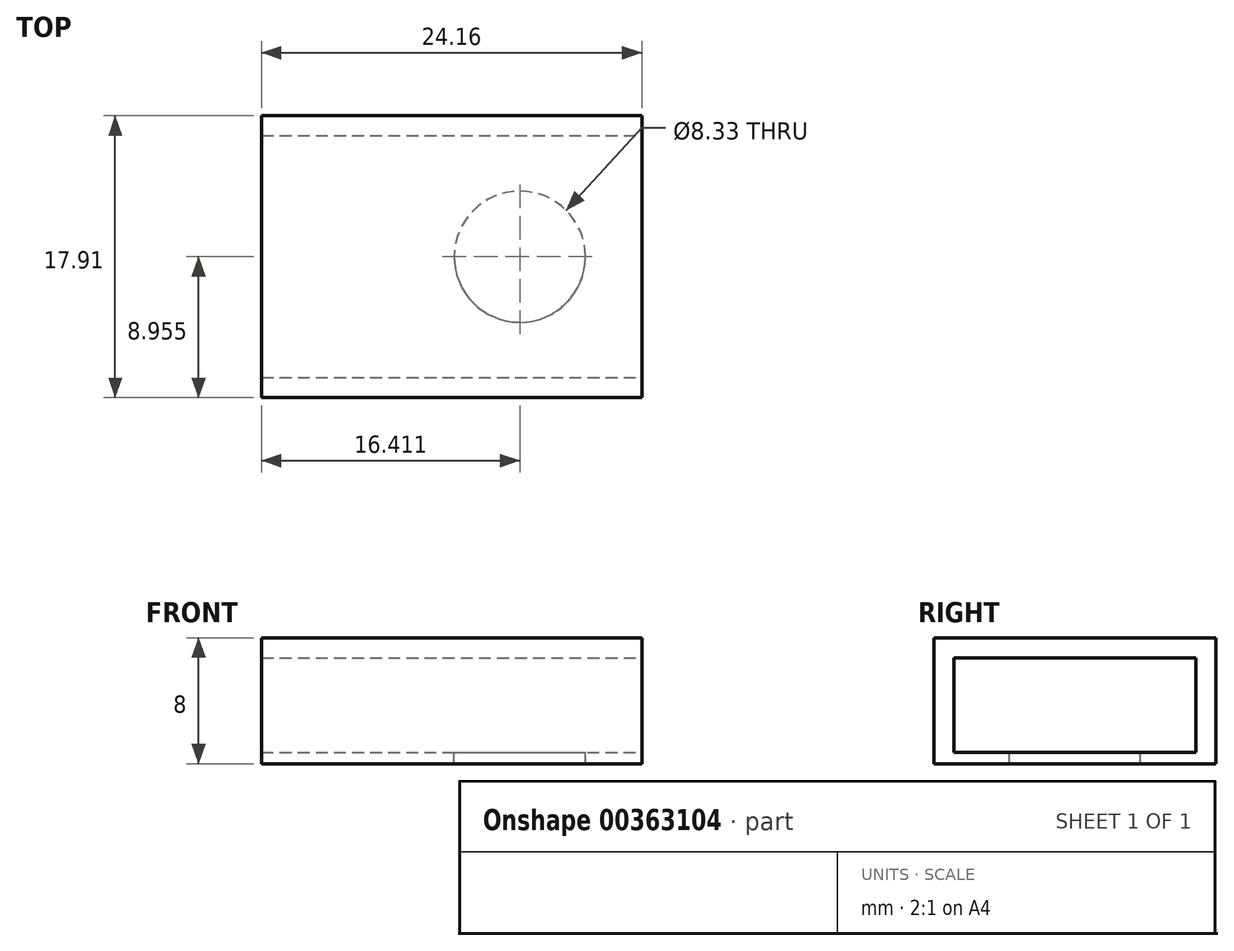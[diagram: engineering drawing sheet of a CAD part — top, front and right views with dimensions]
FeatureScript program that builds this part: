
annotation { "Feature Type Name" : "Feature", "Feature Type Description" : "" }
export const myFeature = defineFeature(function(context is Context, id is Id, definition is map)
    precondition{}
    {
        {
            var Q0;
            Q0=qCreatedBy(makeId("Top.planeOp"),FACE);
            var sketch = newSketch(context, id + "F0", { "sketchPlane" : qUnion([Q0])});
            skLineSegment(sketch, "E0.bottom", {"start": v(-52.08, 35.53) * mm, "end": v(-27.93, 35.53) * mm});
            skLineSegment(sketch, "E0.top", {"start": v(-52.08, 17.62) * mm, "end": v(-27.93, 17.62) * mm});
            skLineSegment(sketch, "E0.left", {"start": v(-52.08, 35.53) * mm, "end": v(-52.08, 17.62) * mm});
            skLineSegment(sketch, "E0.right", {"start": v(-27.93, 35.53) * mm, "end": v(-27.93, 17.62) * mm});
            skSolve(sketch);
        }
        {
            var Q0;
            Q0=makeQuery(id+"F0.imprint","IMPRINT",FACE,{"disambiguationData":[TD([[makeQuery(id+"F0.imprint","IMPRINT",EDGE,{"derivedFrom":sQuery(id+"F0.wireOp",EDGE,"E0.bottom")}),-1.0]])]});
            extrude(context, id + "F1", {"entities" : qUnion([Q0]), "depth" : 4.57 * mm});
        }
        {
            var Q0;
            Q0=qCreatedBy(makeId("Top.planeOp"),FACE);
            var sketch = newSketch(context, id + "F2", { "sketchPlane" : qUnion([Q0])});
            skLineSegment(sketch, "E1.bottom", {"start": v(-52.08, 35.53) * mm, "end": v(-27.93, 35.53) * mm});
            skLineSegment(sketch, "E1.top", {"start": v(-52.08, 34.26) * mm, "end": v(-27.93, 34.26) * mm});
            skLineSegment(sketch, "E1.left", {"start": v(-52.08, 35.53) * mm, "end": v(-52.08, 34.26) * mm});
            skLineSegment(sketch, "E1.right", {"start": v(-27.93, 35.53) * mm, "end": v(-27.93, 34.26) * mm});
            skLineSegment(sketch, "E2.bottom", {"start": v(-52.08, 18.9) * mm, "end": v(-27.93, 18.9) * mm});
            skLineSegment(sketch, "E2.top", {"start": v(-52.08, 17.63) * mm, "end": v(-27.93, 17.63) * mm});
            skLineSegment(sketch, "E2.left", {"start": v(-52.08, 18.9) * mm, "end": v(-52.08, 17.63) * mm});
            skLineSegment(sketch, "E2.right", {"start": v(-27.93, 18.9) * mm, "end": v(-27.93, 17.63) * mm});
            skSolve(sketch);
        }
        {
            var Q0;
            Q0=sQuery(id+"F2.wireOp",EDGE,"E1.bottom");
            var Q1;
            Q1=sQuery(id+"F2.wireOp",EDGE,"E1.top");
            var Q2;
            Q2=sQuery(id+"F2.wireOp",EDGE,"E2.bottom");
            var Q3;
            Q3=sQuery(id+"F2.wireOp",EDGE,"E2.top");
            var Q4;
            Q4=sQuery(id+"F2.wireOp",EDGE,"E2.right");
            var Q5;
            Q5=sQuery(id+"F2.wireOp",EDGE,"E1.left");
            var Q6;
            Q6=sQuery(id+"F2.wireOp",EDGE,"E1.right");
            var Q7;
            Q7=sQuery(id+"F2.wireOp",EDGE,"E2.left");
            extrude(context, id + "F3", {"bodyType" : ToolBodyType.SURFACE, "surfaceEntities" : qUnion([Q0, Q1, Q2, Q3, Q4, Q5, Q6, Q7]), "oppositeDirection" : true, "depth" : 2.72 * mm});
        }
        {
            var Q0;
            Q0=qCreatedBy(makeId("Top.planeOp"),FACE);
            var sketch = newSketch(context, id + "F4", { "sketchPlane" : qUnion([Q0])});
            skLineSegment(sketch, "E3.bottom", {"start": v(-52.09, 17.62) * mm, "end": v(-27.93, 17.62) * mm});
            skLineSegment(sketch, "E3.top", {"start": v(-52.09, 35.53) * mm, "end": v(-27.93, 35.53) * mm});
            skLineSegment(sketch, "E3.left", {"start": v(-52.09, 17.62) * mm, "end": v(-52.09, 35.53) * mm});
            skLineSegment(sketch, "E3.right", {"start": v(-27.93, 17.62) * mm, "end": v(-27.93, 35.53) * mm});
            skSolve(sketch);
        }
        {
            var Q0;
            Q0 = qSketchRegion(id + "F4", true);
            extrude(context, id + "F5", {"entities" : qUnion([Q0]), "operationType" : NewBodyOperationType.ADD, "oppositeDirection" : true, "depth" : 3.43 * mm});
        }
        {
            var Q0;
            Q0=qCreatedBy(makeId("Right.planeOp"),FACE);
            var sketch = newSketch(context, id + "F6", { "sketchPlane" : qUnion([Q0])});
            skLineSegment(sketch, "E4.bottom", {"start": v(18.9, 3.3) * mm, "end": v(34.26, 3.3) * mm});
            skLineSegment(sketch, "E4.top", {"start": v(18.9, -2.72) * mm, "end": v(34.26, -2.72) * mm});
            skLineSegment(sketch, "E4.left", {"start": v(18.9, 3.3) * mm, "end": v(18.9, -2.72) * mm});
            skLineSegment(sketch, "E4.right", {"start": v(34.26, 3.3) * mm, "end": v(34.26, -2.72) * mm});
            skSolve(sketch);
        }
        {
            var Q0;
            Q0 = qSketchRegion(id + "F6", true);
            extrude(context, id + "F7", {"entities" : qUnion([Q0]), "operationType" : NewBodyOperationType.REMOVE, "endBound" : BoundingType.THROUGH_ALL, "oppositeDirection" : true, "depth" : 25.4 * mm});
        }
        {
            var Q0;
            Q0=qCreatedBy(makeId("Top.planeOp"),FACE);
            var sketch = newSketch(context, id + "F8", { "sketchPlane" : qUnion([Q0])});
            skCircle(sketch, "E5", {"center": v(-35.68, 26.58) * mm, "radius": 4.17 * mm});
            skLineSegment(sketch, "E6", {"start": v(-35.68, 17.62) * mm, "end": v(-35.68, 35.53) * mm});
            skLineSegment(sketch, "E7", {"start": v(-52.09, 26.58) * mm, "end": v(-27.93, 26.58) * mm});
            skSolve(sketch);
        }
        {
            var Q0;
            Q0 = qSketchRegion(id + "F8", true);
            extrude(context, id + "F9", {"entities" : qUnion([Q0]), "operationType" : NewBodyOperationType.REMOVE, "oppositeDirection" : true, "depth" : 25.4 * mm});
        }
    });
